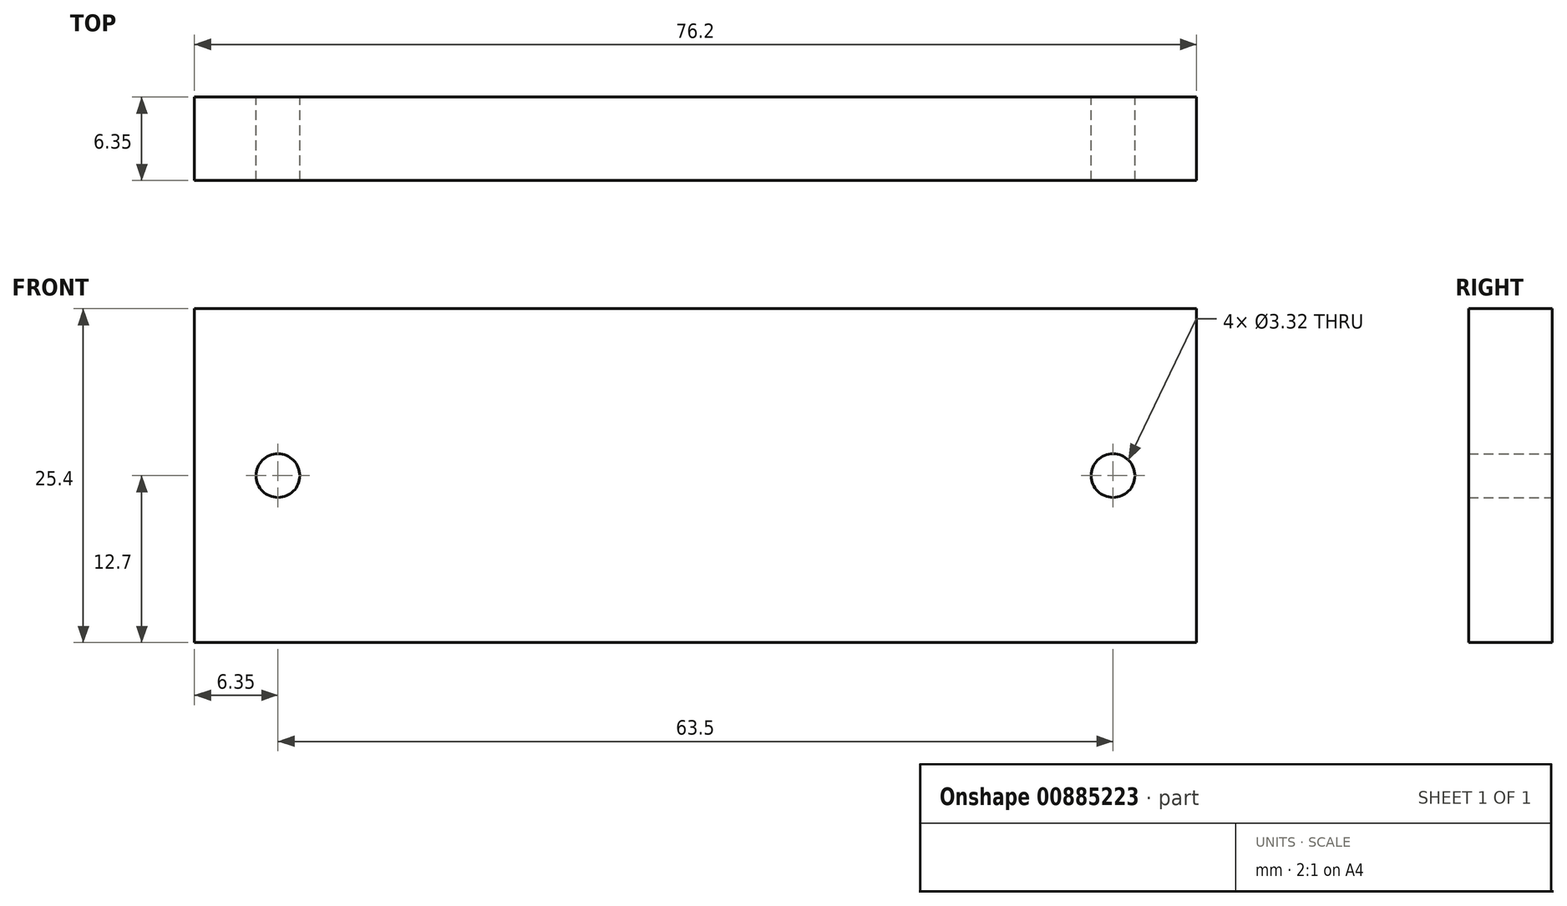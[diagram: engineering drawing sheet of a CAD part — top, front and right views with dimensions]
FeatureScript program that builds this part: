
annotation { "Feature Type Name" : "Feature", "Feature Type Description" : "" }
export const myFeature = defineFeature(function(context is Context, id is Id, definition is map)
    precondition{}
    {
        {
            var Q0;
            Q0=qCreatedBy(makeId("Front.planeOp"),FACE);
            var sketch = newSketch(context, id + "F0", { "sketchPlane" : qUnion([Q0])});
            skLineSegment(sketch, "E0.bottom", {"start": v(38.1, 12.7) * mm, "end": v(-38.1, 12.7) * mm});
            skLineSegment(sketch, "E0.top", {"start": v(38.1, -12.7) * mm, "end": v(-38.1, -12.7) * mm});
            skLineSegment(sketch, "E0.left", {"start": v(38.1, 12.7) * mm, "end": v(38.1, -12.7) * mm});
            skLineSegment(sketch, "E0.right", {"start": v(-38.1, 12.7) * mm, "end": v(-38.1, -12.7) * mm});
            skPoint(sketch, "E0.middle", {"position": v(0, 0) * mm});
            skCircle(sketch, "E1", {"center": v(-31.75, 0) * mm, "radius": 1.66 * mm});
            skLineSegment(sketch, "E2", {"start": v(0, -24.53) * mm, "end": v(0, 21.11) * mm, "construction": true});
            skCircle(sketch, "E3.MirrorC", {"center": v(31.75, 0) * mm, "radius": 1.66 * mm});
            skSolve(sketch);
        }
        {
            var Q0;
            Q0=makeQuery(id+"F0.imprint","IMPRINT",FACE,{"disambiguationData":[TD([[makeQuery(id+"F0.imprint","IMPRINT",EDGE,{"derivedFrom":sQuery(id+"F0.wireOp",EDGE,"E0.bottom")}),1.0]])]});
            extrude(context, id + "F1", {"entities" : qUnion([Q0]), "depth" : 6.35 * mm, "offsetDistance" : 25.4 * mm});
        }
    });
